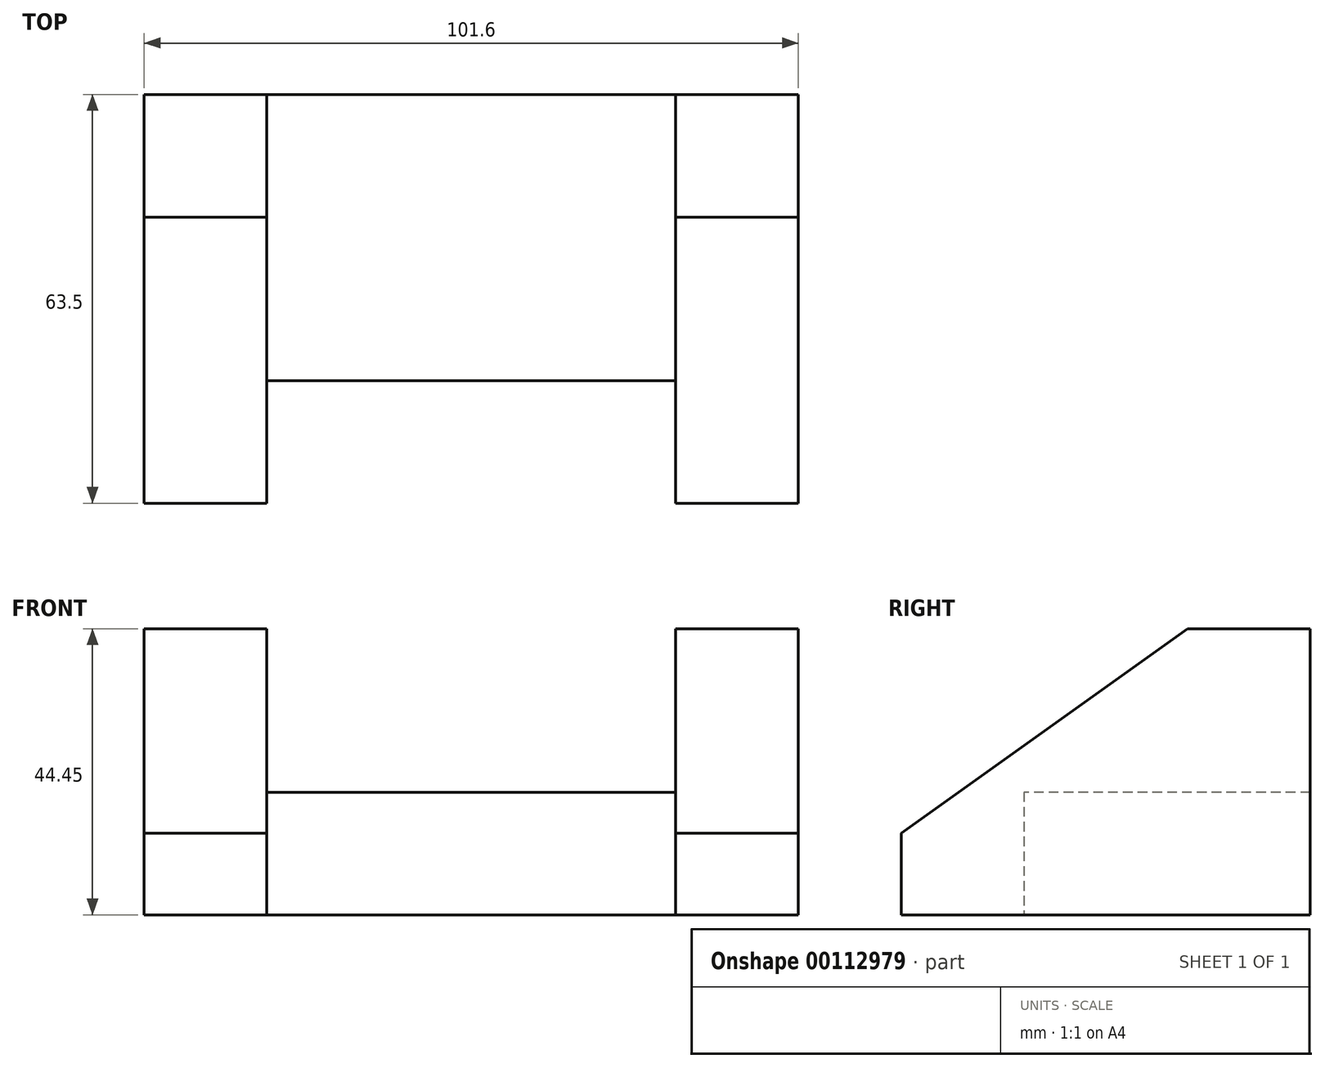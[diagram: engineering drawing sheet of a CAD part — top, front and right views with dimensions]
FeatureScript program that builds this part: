
annotation { "Feature Type Name" : "Feature", "Feature Type Description" : "" }
export const myFeature = defineFeature(function(context is Context, id is Id, definition is map)
    precondition{}
    {
        {
            var Q0;
            Q0=qCreatedBy(makeId("Right.planeOp"),FACE);
            var sketch = newSketch(context, id + "F0", { "sketchPlane" : qUnion([Q0])});
            skLineSegment(sketch, "E0", {"start": v(0, 0) * mm, "end": v(0, 12.7) * mm});
            skLineSegment(sketch, "E1", {"start": v(0, 0) * mm, "end": v(63.5, 0) * mm});
            skLineSegment(sketch, "E2", {"start": v(63.5, 0) * mm, "end": v(63.5, 44.45) * mm});
            skLineSegment(sketch, "E3", {"start": v(63.5, 44.45) * mm, "end": v(44.45, 44.45) * mm});
            skLineSegment(sketch, "E4", {"start": v(44.45, 44.45) * mm, "end": v(0, 12.7) * mm});
            skSolve(sketch);
        }
        {
            var Q0;
            Q0 = qSketchRegion(id + "F0", true);
            extrude(context, id + "F1", {"entities" : qUnion([Q0]), "oppositeDirection" : true, "depth" : 19.05 * mm});
        }
        {
            var Q0;
            Q0=makeQuery(id+"F1.opExtrude","CAP_FACE",FACE,{"disambiguationData":[OSD([sQuery(id+"F0.wireOp",EDGE,"E0"),sQuery(id+"F0.wireOp",EDGE,"E1"),sQuery(id+"F0.wireOp",EDGE,"E2"),sQuery(id+"F0.wireOp",EDGE,"E3"),sQuery(id+"F0.wireOp",EDGE,"E4")])],"isStart":false});
            var sketch = newSketch(context, id + "F2", { "sketchPlane" : qUnion([Q0])});
            skLineSegment(sketch, "E5", {"start": v(-63.5, 0) * mm, "end": v(-63.5, 19.05) * mm});
            skLineSegment(sketch, "E6", {"start": v(-63.5, 19.05) * mm, "end": v(-19.05, 19.05) * mm});
            skLineSegment(sketch, "E7", {"start": v(-19.05, 19.05) * mm, "end": v(-19.05, 0) * mm});
            skLineSegment(sketch, "E8", {"start": v(-19.05, 0) * mm, "end": v(-63.5, 0) * mm});
            skSolve(sketch);
        }
        {
            var Q0;
            Q0 = qSketchRegion(id + "F2", true);
            extrude(context, id + "F3", {"entities" : qUnion([Q0]), "operationType" : NewBodyOperationType.ADD, "depth" : 63.5 * mm});
        }
        {
            var Q0;
            Q0=makeQuery(id+"F3.opExtrude","CAP_FACE",FACE,{"disambiguationData":[OSD([sQuery(id+"F2.wireOp",EDGE,"E5"),sQuery(id+"F2.wireOp",EDGE,"E6"),sQuery(id+"F2.wireOp",EDGE,"E7"),sQuery(id+"F2.wireOp",EDGE,"E8")])],"isStart":false});
            var sketch = newSketch(context, id + "F4", { "sketchPlane" : qUnion([Q0])});
            skLineSegment(sketch, "E9", {"start": v(-63.5, 0) * mm, "end": v(-63.5, 44.45) * mm});
            skLineSegment(sketch, "E10", {"start": v(-63.5, 44.45) * mm, "end": v(-44.45, 44.45) * mm});
            skLineSegment(sketch, "E11", {"start": v(-63.5, 0) * mm, "end": v(0, 0) * mm});
            skLineSegment(sketch, "E12", {"start": v(0, 0) * mm, "end": v(0, 12.7) * mm});
            skLineSegment(sketch, "E13", {"start": v(0, 12.7) * mm, "end": v(-44.45, 44.45) * mm});
            skSolve(sketch);
        }
        {
            var Q0;
            Q0 = qSketchRegion(id + "F4", true);
            extrude(context, id + "F5", {"entities" : qUnion([Q0]), "operationType" : NewBodyOperationType.ADD, "depth" : 19.05 * mm});
        }
    });
